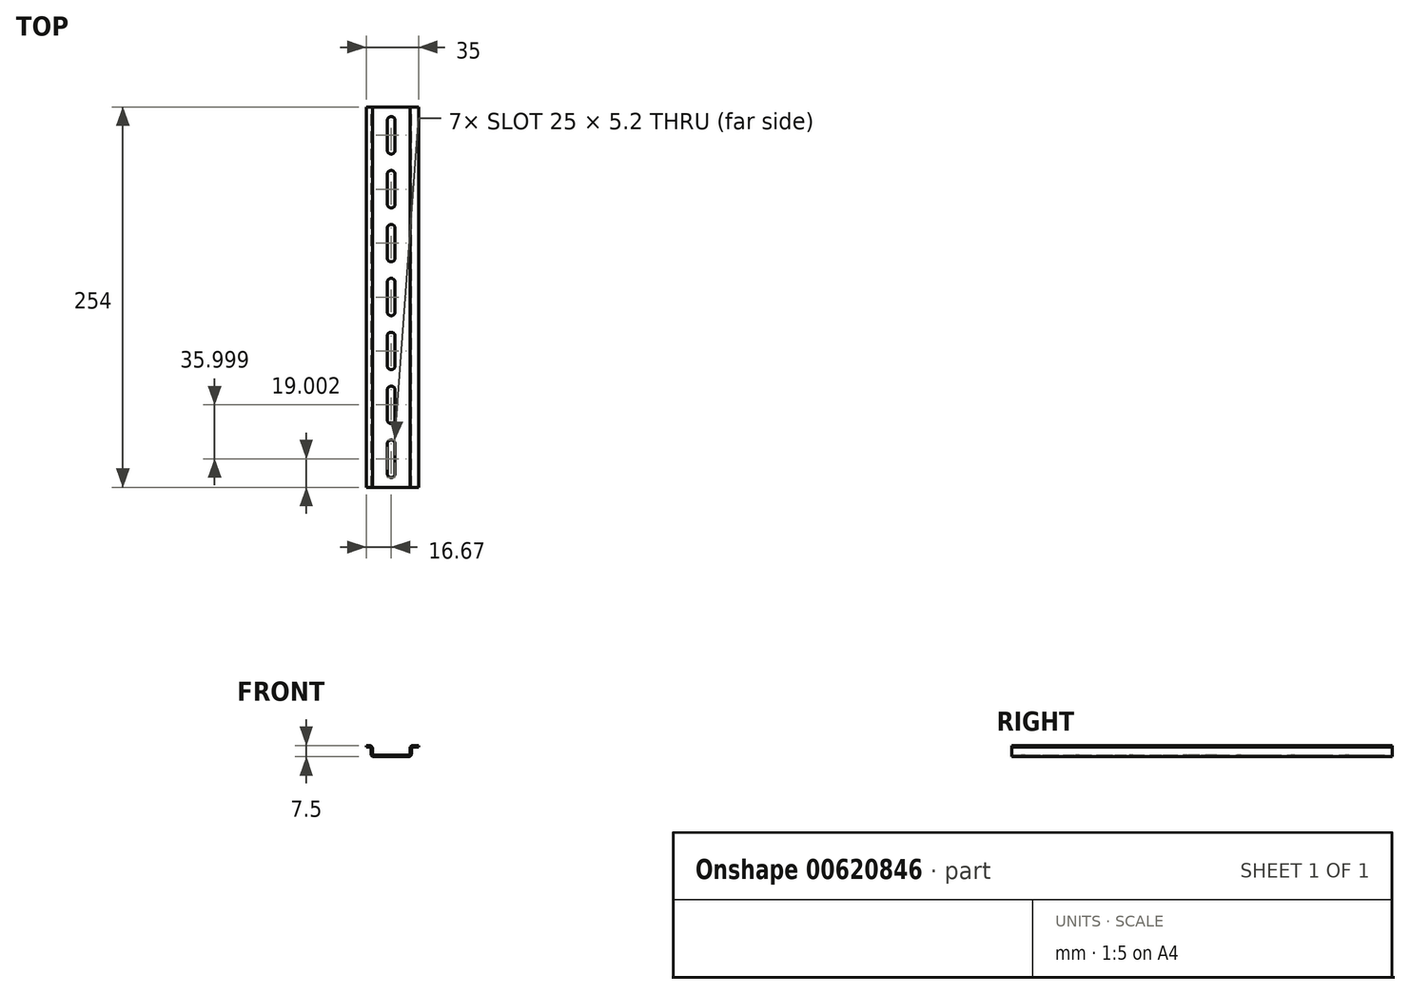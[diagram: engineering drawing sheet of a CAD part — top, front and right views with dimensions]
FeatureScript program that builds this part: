
annotation { "Feature Type Name" : "Feature", "Feature Type Description" : "" }
export const myFeature = defineFeature(function(context is Context, id is Id, definition is map)
    precondition{}
    {
        {
            var Q0;
            Q0=qCreatedBy(makeId("Front.planeOp"),FACE);
            var sketch = newSketch(context, id + "F0", { "sketchPlane" : qUnion([Q0])});
            skLineSegment(sketch, "E0", {"start": v(-11.5, 0) * mm, "end": v(11.5, 0) * mm});
            skLineSegment(sketch, "E1", {"start": v(13.5, 2) * mm, "end": v(13.5, 5.5) * mm});
            skLineSegment(sketch, "E2", {"start": v(14.5, 6.5) * mm, "end": v(18.33, 6.5) * mm});
            skLineSegment(sketch, "E3", {"start": v(18.33, 6.5) * mm, "end": v(18.33, 7.5) * mm});
            skLineSegment(sketch, "E4", {"start": v(18.33, 7.5) * mm, "end": v(14.52, 7.5) * mm});
            skLineSegment(sketch, "E5", {"start": v(12.52, 5.5) * mm, "end": v(12.52, 2) * mm});
            skLineSegment(sketch, "E6", {"start": v(11.52, 1) * mm, "end": v(-11.48, 1) * mm});
            skLineSegment(sketch, "E7", {"start": v(-12.48, 2) * mm, "end": v(-12.48, 5.5) * mm});
            skLineSegment(sketch, "E8", {"start": v(-14.48, 7.5) * mm, "end": v(-16.67, 7.5) * mm});
            skLineSegment(sketch, "E9", {"start": v(-16.67, 7.5) * mm, "end": v(-16.67, 6.5) * mm});
            skLineSegment(sketch, "E10", {"start": v(-16.67, 6.5) * mm, "end": v(-14.5, 6.5) * mm});
            skLineSegment(sketch, "E11", {"start": v(-13.5, 5.5) * mm, "end": v(-13.5, 2) * mm});
            skPoint(sketch, "E12.visualSharp", {"position": v(-12.48, 1) * mm});
            skArc(sketch, "E12.filletArc", {"start": v(-12.48, 2) * mm, "mid": v(-12.2, 1.3) * mm, "end": v(-11.48, 1) * mm});
            skPoint(sketch, "E13.visualSharp", {"position": v(12.52, 1) * mm});
            skArc(sketch, "E13.filletArc", {"start": v(11.52, 1) * mm, "mid": v(12.22, 1.3) * mm, "end": v(12.52, 2) * mm});
            skPoint(sketch, "E14.visualSharp", {"position": v(13.5, 6.5) * mm});
            skArc(sketch, "E14.filletArc", {"start": v(14.5, 6.5) * mm, "mid": v(13.8, 6.2) * mm, "end": v(13.5, 5.5) * mm});
            skPoint(sketch, "E15.visualSharp", {"position": v(-13.5, 6.5) * mm});
            skArc(sketch, "E15.filletArc", {"start": v(-13.5, 5.5) * mm, "mid": v(-13.8, 6.2) * mm, "end": v(-14.5, 6.5) * mm});
            skPoint(sketch, "E16.visualSharp", {"position": v(12.52, 7.5) * mm});
            skArc(sketch, "E16.filletArc", {"start": v(14.52, 7.5) * mm, "mid": v(13.1, 6.92) * mm, "end": v(12.52, 5.5) * mm});
            skPoint(sketch, "E17.visualSharp", {"position": v(13.5, 0) * mm});
            skArc(sketch, "E17.filletArc", {"start": v(11.5, 0) * mm, "mid": v(12.91, 0.59) * mm, "end": v(13.5, 2) * mm});
            skPoint(sketch, "E18.visualSharp", {"position": v(-13.5, 0) * mm});
            skArc(sketch, "E18.filletArc", {"start": v(-13.5, 2) * mm, "mid": v(-12.91, 0.59) * mm, "end": v(-11.5, 0) * mm});
            skPoint(sketch, "E19.visualSharp", {"position": v(-12.48, 7.5) * mm});
            skArc(sketch, "E19.filletArc", {"start": v(-12.48, 5.5) * mm, "mid": v(-13.07, 6.92) * mm, "end": v(-14.48, 7.5) * mm});
            skSolve(sketch);
        }
        {
            var Q0;
            Q0=qSketchRegion(id+"F0",true);
            extrude(context, id + "F1", {"entities" : qUnion([Q0]), "endBound" : BoundingType.SYMMETRIC, "depth" : 254 * mm, "offsetDistance" : 25 * mm});
        }
        {
            var Q0;
            Q0=makeQuery(id+"F1.opExtrude","SWEPT_FACE",FACE,{"disambiguationData":[OSD([sQuery(id+"F0.wireOp",EDGE,"E6")])]});
            var sketch = newSketch(context, id + "F2", { "sketchPlane" : qUnion([Q0])});
            skLineSegment(sketch, "E20", {"start": v(-2.6, 9.9) * mm, "end": v(-2.6, -9.9) * mm});
            skArc(sketch, "E21", {"start": v(-2.6, -9.9) * mm, "mid": v(0, -12.5) * mm, "end": v(2.6, -9.9) * mm});
            skLineSegment(sketch, "E22", {"start": v(2.6, -9.9) * mm, "end": v(2.6, 9.9) * mm});
            skArc(sketch, "E23", {"start": v(2.6, 9.9) * mm, "mid": v(0, 12.5) * mm, "end": v(-2.6, 9.9) * mm});
            skLineSegment(sketch, "E24", {"start": v(2.6, 26.1) * mm, "end": v(2.6, 45.9) * mm});
            skLineSegment(sketch, "E25", {"start": v(-2.6, 45.9) * mm, "end": v(-2.6, 26.1) * mm});
            skArc(sketch, "E26", {"start": v(2.6, 45.9) * mm, "mid": v(0, 48.5) * mm, "end": v(-2.6, 45.9) * mm});
            skArc(sketch, "E27", {"start": v(-2.6, 26.1) * mm, "mid": v(0, 23.5) * mm, "end": v(2.6, 26.1) * mm});
            skLineSegment(sketch, "E28", {"start": v(2.6, 62.1) * mm, "end": v(2.6, 81.9) * mm});
            skLineSegment(sketch, "E29", {"start": v(-2.6, 81.9) * mm, "end": v(-2.6, 62.1) * mm});
            skArc(sketch, "E30", {"start": v(2.6, 81.9) * mm, "mid": v(0, 84.5) * mm, "end": v(-2.6, 81.9) * mm});
            skArc(sketch, "E31", {"start": v(-2.6, 62.1) * mm, "mid": v(0, 59.5) * mm, "end": v(2.6, 62.1) * mm});
            skLineSegment(sketch, "E32", {"start": v(2.6, 98.1) * mm, "end": v(2.6, 117.9) * mm});
            skLineSegment(sketch, "E33", {"start": v(-2.6, 117.9) * mm, "end": v(-2.6, 98.1) * mm});
            skArc(sketch, "E34", {"start": v(2.6, 117.9) * mm, "mid": v(0, 120.5) * mm, "end": v(-2.6, 117.9) * mm});
            skArc(sketch, "E35", {"start": v(-2.6, 98.1) * mm, "mid": v(0, 95.5) * mm, "end": v(2.6, 98.1) * mm});
            skLineSegment(sketch, "E36", {"start": v(2.6, -45.9) * mm, "end": v(2.6, -26.1) * mm});
            skLineSegment(sketch, "E37", {"start": v(-2.6, -26.1) * mm, "end": v(-2.6, -45.9) * mm});
            skArc(sketch, "E38", {"start": v(2.6, -26.1) * mm, "mid": v(0, -23.5) * mm, "end": v(-2.6, -26.1) * mm});
            skArc(sketch, "E39", {"start": v(-2.6, -45.9) * mm, "mid": v(0, -48.5) * mm, "end": v(2.6, -45.9) * mm});
            skLineSegment(sketch, "E40", {"start": v(2.6, -81.9) * mm, "end": v(2.6, -62.1) * mm});
            skLineSegment(sketch, "E41", {"start": v(-2.6, -62.1) * mm, "end": v(-2.6, -81.9) * mm});
            skArc(sketch, "E42", {"start": v(2.6, -62.1) * mm, "mid": v(0, -59.5) * mm, "end": v(-2.6, -62.1) * mm});
            skArc(sketch, "E43", {"start": v(-2.6, -81.9) * mm, "mid": v(0, -84.5) * mm, "end": v(2.6, -81.9) * mm});
            skLineSegment(sketch, "E44", {"start": v(2.6, -117.9) * mm, "end": v(2.6, -98.1) * mm});
            skLineSegment(sketch, "E45", {"start": v(-2.6, -98.1) * mm, "end": v(-2.6, -117.9) * mm});
            skArc(sketch, "E46", {"start": v(2.6, -98.1) * mm, "mid": v(0, -95.5) * mm, "end": v(-2.6, -98.1) * mm});
            skArc(sketch, "E47", {"start": v(-2.6, -117.9) * mm, "mid": v(0, -120.5) * mm, "end": v(2.6, -117.9) * mm});
            skSolve(sketch);
        }
        {
            var Q0;
            Q0=qSketchRegion(id+"F2",true);
            extrude(context, id + "F3", {"entities" : qUnion([Q0]), "operationType" : NewBodyOperationType.REMOVE, "endBound" : BoundingType.THROUGH_ALL, "oppositeDirection" : true, "depth" : 25.4 * mm, "offsetDistance" : 25 * mm});
        }
    });
